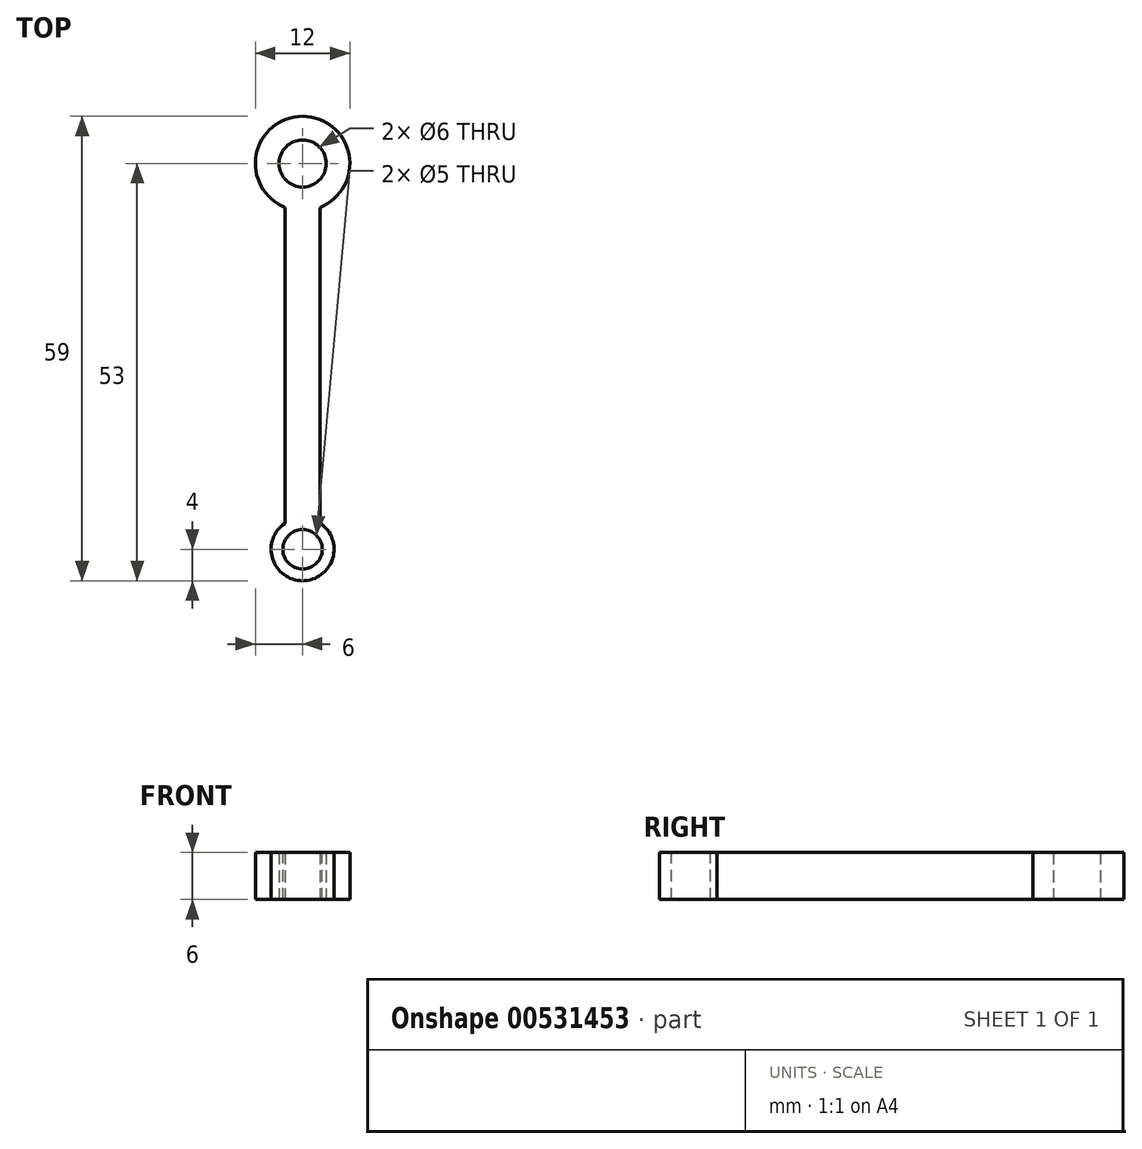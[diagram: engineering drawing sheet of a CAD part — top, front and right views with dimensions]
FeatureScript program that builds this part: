
annotation { "Feature Type Name" : "Feature", "Feature Type Description" : "" }
export const myFeature = defineFeature(function(context is Context, id is Id, definition is map)
    precondition{}
    {
        {
            var Q0;
            Q0=qCreatedBy(makeId("Top.planeOp"),FACE);
            var sketch = newSketch(context, id + "F0", { "sketchPlane" : qUnion([Q0])});
            skArc(sketch, "E0", {"start": v(-2.25, 3.3) * mm, "mid": v(0, -4) * mm, "end": v(2.25, 3.3) * mm});
            skArc(sketch, "E1", {"start": v(2.25, 43.44) * mm, "mid": v(0, 55) * mm, "end": v(-2.25, 43.44) * mm});
            skLineSegment(sketch, "E2", {"start": v(-2.25, 43.44) * mm, "end": v(-2.25, 3.3) * mm});
            skLineSegment(sketch, "E3", {"start": v(2.25, 43.44) * mm, "end": v(2.25, 3.3) * mm});
            skCircle(sketch, "E4", {"center": v(0, 49) * mm, "radius": 3 * mm});
            skCircle(sketch, "E5", {"center": v(0, 0) * mm, "radius": 2 * mm});
            skSolve(sketch);
        }
        {
            var Q0;
            Q0=qSketchRegion(id+"F0",true);
            extrude(context, id + "F1", {"entities" : qUnion([Q0]), "depth" : 6 * mm, "offsetDistance" : 25 * mm});
        }
        {
            var Q0;
            Q0=makeQuery(id+"F1.opExtrude","CAP_FACE",FACE,{"disambiguationData":[OSD([sQuery(id+"F0.wireOp",EDGE,"E0"),sQuery(id+"F0.wireOp",EDGE,"E1"),sQuery(id+"F0.wireOp",EDGE,"E2"),sQuery(id+"F0.wireOp",EDGE,"E3"),sQuery(id+"F0.wireOp",EDGE,"E4"),sQuery(id+"F0.wireOp",EDGE,"9ayo6xkF-RkV7-GW2R-E9bK-3cueWKfAAzvc"),sQuery(id+"F0.wireOp",EDGE,"QLvp9qMP-qnWA-Y4zr-RQRT-3W7DafZWEicE"),sQuery(id+"F0.wireOp",EDGE,"xG4LSZlB-o8Cn-KnOt-qgaa-vAlnUjY95cmA"),sQuery(id+"F0.wireOp",EDGE,"BogJxpM3-jV2k-MuWz-DKha-7LKbdoNA0O7A")])],"isStart":false});
            var sketch = newSketch(context, id + "F2", { "sketchPlane" : qUnion([Q0])});
            skCircle(sketch, "E6", {"center": v(0, 0) * mm, "radius": 2.5 * mm});
            skSolve(sketch);
        }
        {
            var Q0;
            Q0=qSketchRegion(id+"F2",true);
            extrude(context, id + "F3", {"entities" : qUnion([Q0]), "operationType" : NewBodyOperationType.REMOVE, "oppositeDirection" : true, "depth" : 8.1 * mm, "offsetDistance" : 25 * mm});
        }
    });
